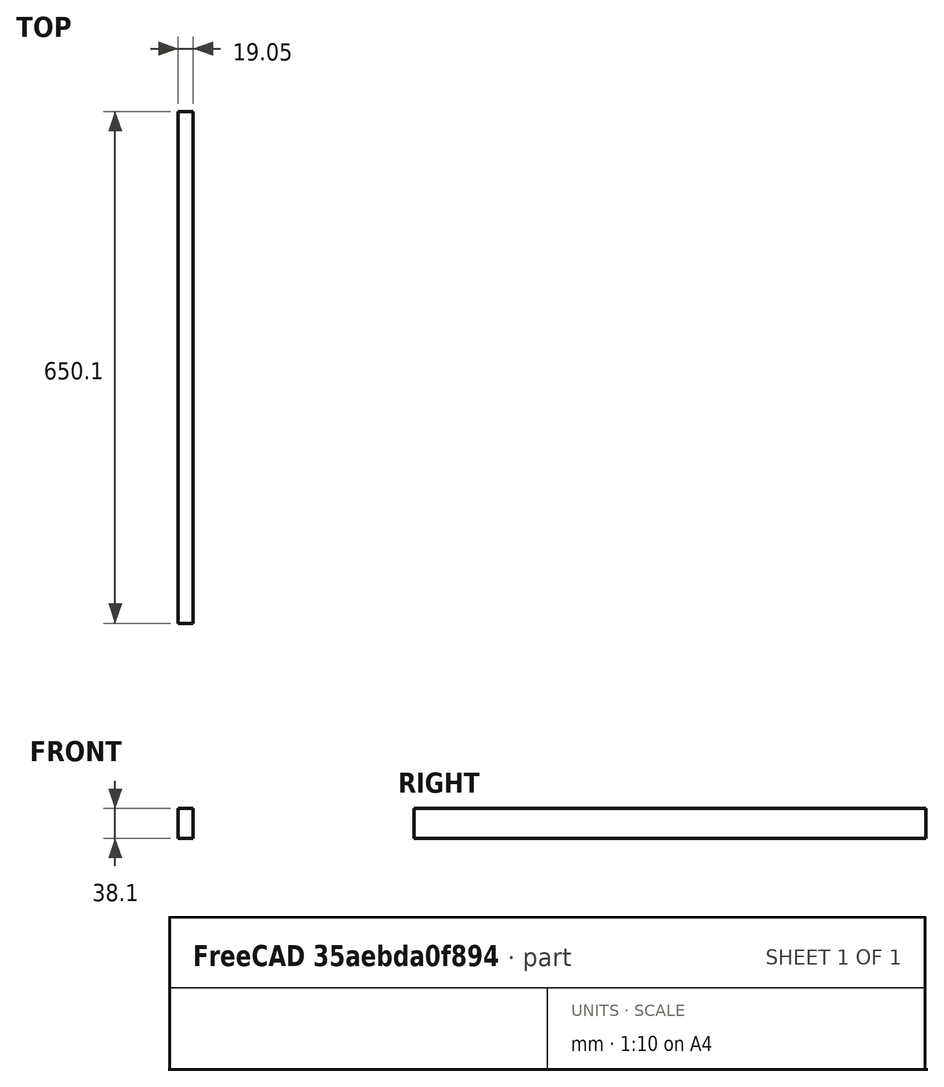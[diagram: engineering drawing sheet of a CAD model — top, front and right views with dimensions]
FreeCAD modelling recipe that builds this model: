
FCSTD DOCUMENT  (FreeCAD 0.20R29177 (Git))
Label: topLeftSideBand
License: All rights reserved
LicenseURL: http://en.wikipedia.org/wiki/All_rights_reserved
objects: Sketcher::SketchObject×1, PartDesign::Pad×1, PartDesign::Body×1
note: 4 computed .brp shape members not serialized (recipe doc carries the construction recipe); baked Part::Feature solids carry a one-line shape summary decoded from their .brp

FEATURE [Sketcher::SketchObject] Sketch
  FullyConstrained = true
  MapMode = 5
  Placement = pos=(0,0,0) rot=(0.57735,0.57735,0.57735;2.0944rad)
  Support = -> [YZ_Plane]
  expr: Constraints[9] = 1.5 * 25.4
  sketch-geometry (4):
    g0: LineSegment StartX=0 StartY=0 StartZ=0 EndX=650.1 EndY=0 EndZ=0
    g1: LineSegment StartX=650.1 StartY=0 StartZ=0 EndX=650.1 EndY=38.1 EndZ=0
    g2: LineSegment StartX=650.1 StartY=38.1 StartZ=0 EndX=0 EndY=38.1 EndZ=0
    g3: LineSegment StartX=0 StartY=38.1 StartZ=0 EndX=0 EndY=0 EndZ=0
  constraints (11):
    c: Coincident(g0,g1)
    c: Coincident(g1,g2)
    c: Coincident(g2,g3)
    c: Coincident(g3,g0)
    c: Horizontal(g0)
    c: Horizontal(g2)
    c: Vertical(g1)
    c: Vertical(g3)
    c: Coincident(g0,g-1)
    c: DistanceY(g3,g3) = 38.1
    c: DistanceX(g0,g0) = 650.1
FEATURE [PartDesign::Pad] Pad
  Direction = (1,-2e-16,3e-16)
  Length = 19.05
  Length2 = 10
  Placement = pos=(0,0,0) rot=(0.57735,0.57735,0.57735;2.0944rad)
  Profile = -> Sketch
  ReferenceAxis = -> Sketch [N_Axis]
  Type = 0
  expr: Length = 3 / 4 * 25.4
FEATURE [PartDesign::Body] Body
  Group = -> [Sketch,Pad]
  Origin = -> Origin
  Tip = -> Pad
